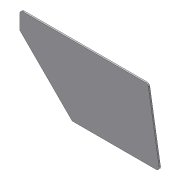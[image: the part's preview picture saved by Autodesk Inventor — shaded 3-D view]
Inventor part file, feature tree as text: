
AUTODESK INVENTOR PART (.ipt)
format: ipt  version: 2012 (Build 160160000, 160)  size: 76,288 bytes
history: native  units: in
note: dims shown in document units (in); Inventor stores cm internally (conversion verified against a paired STEP export)
features: extrude x1, sketch x1
ambient origin geometry x8: Origin, YZ Plane, XZ Plane, XY Plane, X Axis, Y Axis, Z Axis, Center Point
bodies: Solid1 (feature_tree)
feature tree (2):
  extrude  "Extrusion1"  Depth=6.0in
  sketch  "Sketch1"  dims[d0=12.0in d1=6.0in d2=1.0in d3=1.5in d4=7.5in d5=0.25in d6=0.25in d7=0.125in d8=0.0in]
